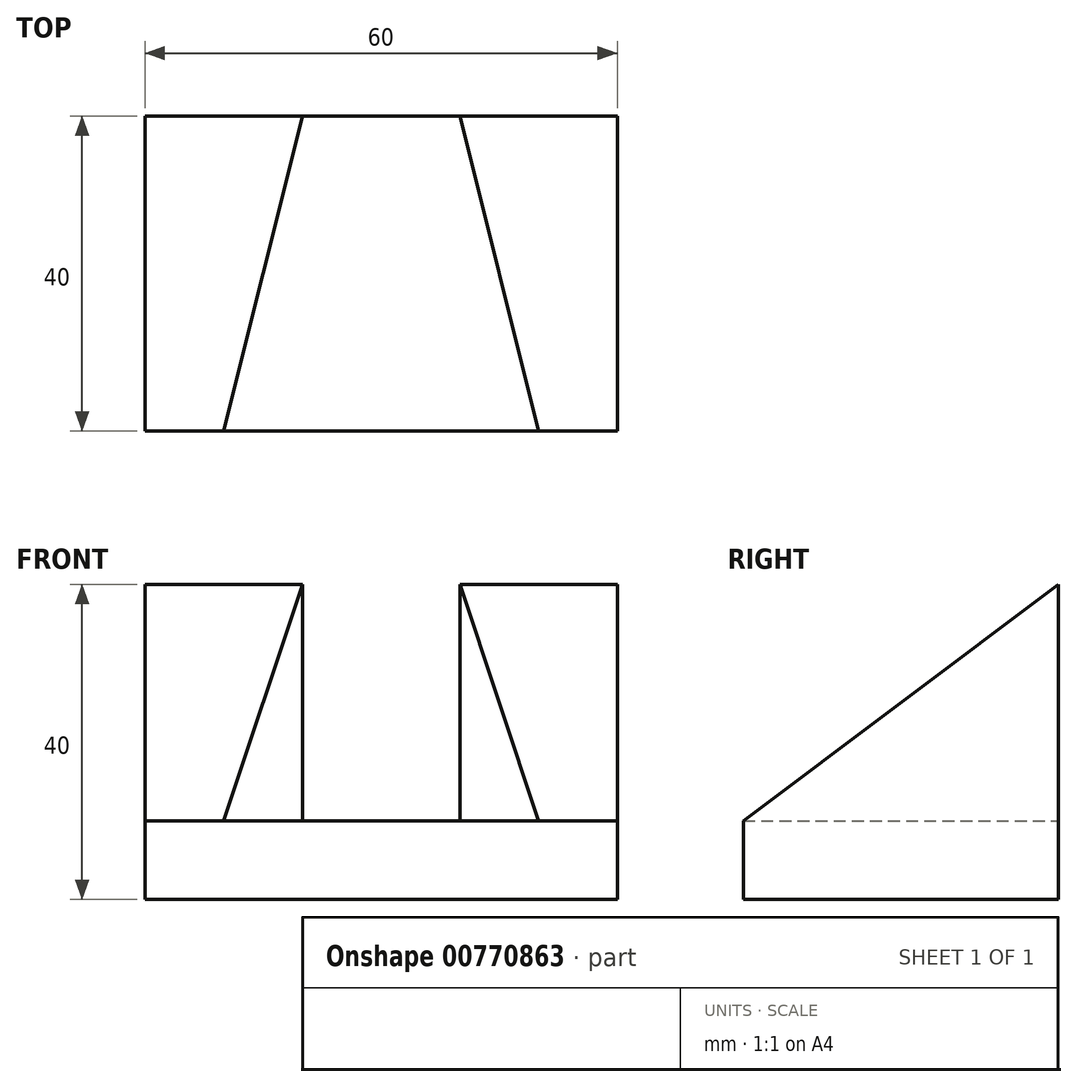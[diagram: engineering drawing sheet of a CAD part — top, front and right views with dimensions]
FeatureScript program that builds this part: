
annotation { "Feature Type Name" : "Feature", "Feature Type Description" : "" }
export const myFeature = defineFeature(function(context is Context, id is Id, definition is map)
    precondition{}
    {
        {
            var Q0;
            Q0=qCreatedBy(makeId("Top.planeOp"),FACE);
            var sketch = newSketch(context, id + "F0", { "sketchPlane" : qUnion([Q0])});
            skLineSegment(sketch, "E0.bottom", {"start": v(-25.56, 14.78) * mm, "end": v(34.44, 14.78) * mm});
            skLineSegment(sketch, "E0.top", {"start": v(-25.56, -25.22) * mm, "end": v(34.44, -25.22) * mm});
            skLineSegment(sketch, "E0.left", {"start": v(-25.56, 14.78) * mm, "end": v(-25.56, -25.22) * mm});
            skLineSegment(sketch, "E0.right", {"start": v(34.44, 14.78) * mm, "end": v(34.44, -25.22) * mm});
            skSolve(sketch);
        }
        {
            var Q0;
            Q0 = qSketchRegion(id + "F0", true);
            extrude(context, id + "F1", {"entities" : qUnion([Q0]), "depth" : 40 * mm, "offsetDistance" : 25 * mm});
        }
        {
            var Q0;
            Q0=makeQuery(id+"F1.opExtrude","CAP_FACE",FACE,{"disambiguationData":[OSD([sQuery(id+"F0.wireOp",EDGE,"E0.bottom"),sQuery(id+"F0.wireOp",EDGE,"E0.top"),sQuery(id+"F0.wireOp",EDGE,"E0.left"),sQuery(id+"F0.wireOp",EDGE,"E0.right")])],"isStart":false});
            var sketch = newSketch(context, id + "F2", { "sketchPlane" : qUnion([Q0])});
            skLineSegment(sketch, "E1", {"start": v(-15.56, -25.22) * mm, "end": v(24.44, -25.22) * mm});
            skLineSegment(sketch, "E2", {"start": v(24.44, -25.22) * mm, "end": v(14.44, 14.78) * mm});
            skLineSegment(sketch, "E3", {"start": v(14.44, 14.78) * mm, "end": v(-5.56, 14.78) * mm});
            skLineSegment(sketch, "E4", {"start": v(-5.56, 14.78) * mm, "end": v(-15.56, -25.22) * mm});
            skSolve(sketch);
        }
        {
            var Q0;
            Q0=makeQuery(id+"F2.imprint","IMPRINT",FACE,{"disambiguationData":[TD([[makeQuery(id+"F2.imprint","IMPRINT",EDGE,{"derivedFrom":sQuery(id+"F2.wireOp",EDGE,"E1")}),1.0]])]});
            extrude(context, id + "F3", {"entities" : qUnion([Q0]), "operationType" : NewBodyOperationType.REMOVE, "oppositeDirection" : true, "depth" : 30 * mm, "offsetDistance" : 25 * mm});
        }
        {
            var Q0;
            Q0=makeQuery(id+"F1.opExtrude","SWEPT_FACE",FACE,{"disambiguationData":[OSD([sQuery(id+"F0.wireOp",EDGE,"E0.right")])]});
            var sketch = newSketch(context, id + "F4", { "sketchPlane" : qUnion([Q0])});
            skLineSegment(sketch, "E5", {"start": v(-25.22, 10) * mm, "end": v(14.78, 40) * mm});
            skLineSegment(sketch, "E6", {"start": v(-25.22, 10) * mm, "end": v(-25.22, 40) * mm});
            skLineSegment(sketch, "E7", {"start": v(-25.22, 40) * mm, "end": v(14.78, 40) * mm});
            skSolve(sketch);
        }
        {
            var Q0;
            Q0=makeQuery(id+"F4.imprint","IMPRINT",FACE,{"disambiguationData":[TD([[makeQuery(id+"F4.imprint","IMPRINT",EDGE,{"derivedFrom":sQuery(id+"F4.wireOp",EDGE,"E5")}),1.0]])]});
            extrude(context, id + "F5", {"entities" : qUnion([Q0]), "operationType" : NewBodyOperationType.REMOVE, "oppositeDirection" : true, "depth" : 60 * mm, "offsetDistance" : 25 * mm});
        }
    });
